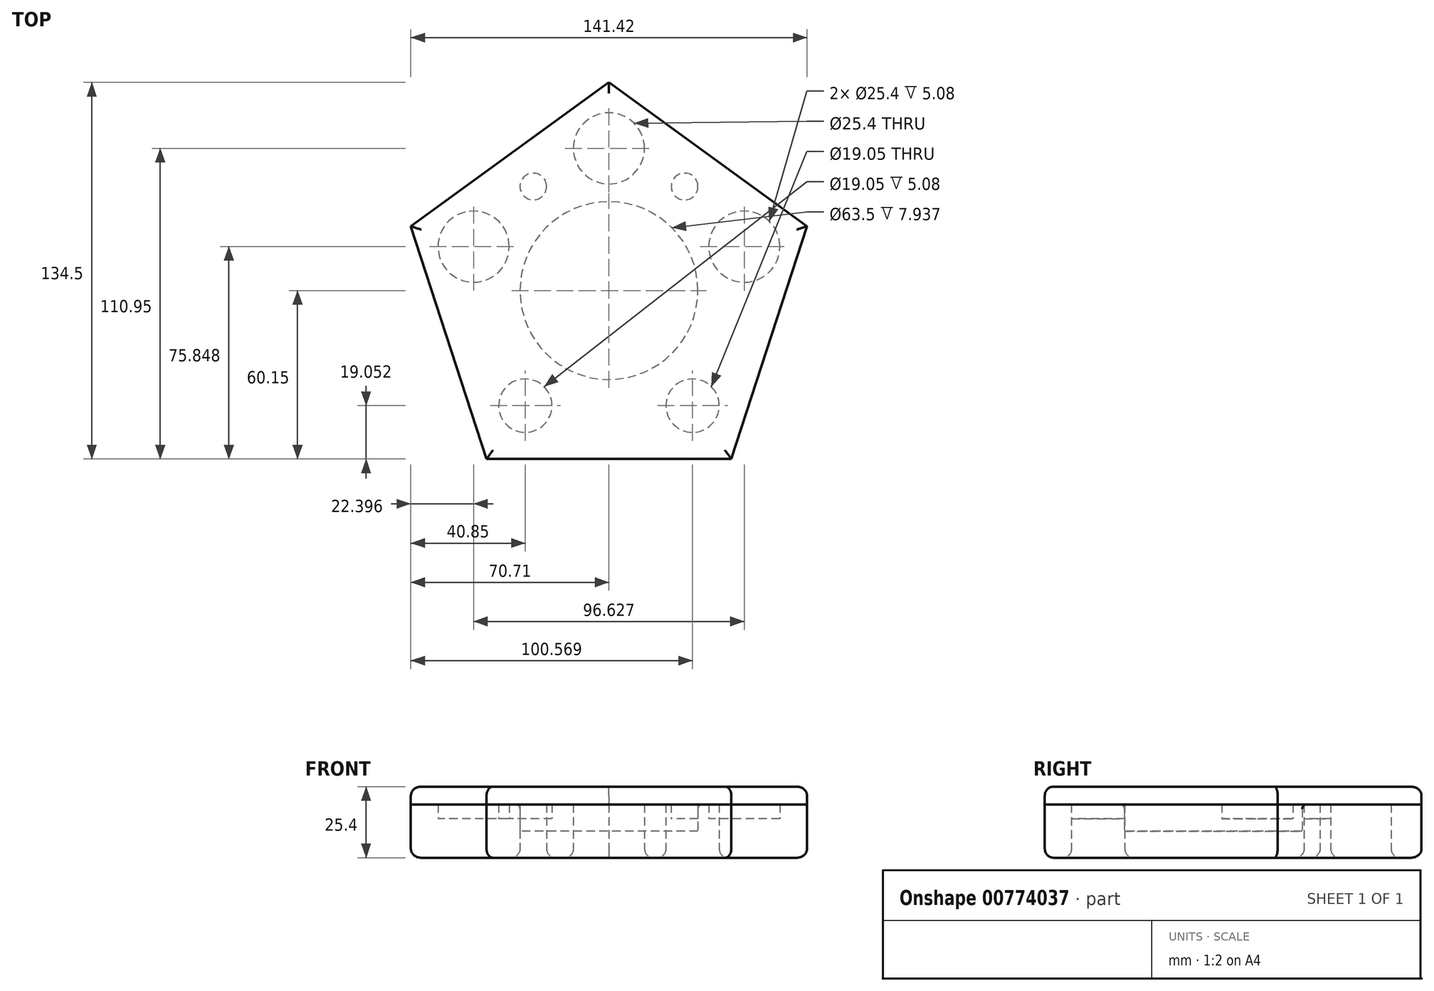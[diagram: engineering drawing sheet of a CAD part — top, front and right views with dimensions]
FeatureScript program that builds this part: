
annotation { "Feature Type Name" : "Feature", "Feature Type Description" : "" }
export const myFeature = defineFeature(function(context is Context, id is Id, definition is map)
    precondition{}
    {
        {
            var Q0;
            Q0=qCreatedBy(makeId("Top.planeOp"),FACE);
            var sketch = newSketch(context, id + "F0", { "sketchPlane" : qUnion([Q0])});
            skLineSegment(sketch, "E0", {"start": v(43.7, -60.15) * mm, "end": v(-43.7, -60.15) * mm});
            skLineSegment(sketch, "E1", {"start": v(-43.7, -60.15) * mm, "end": v(-70.7, 22.97) * mm});
            skLineSegment(sketch, "E2", {"start": v(-70.7, 22.97) * mm, "end": v(0, 74.35) * mm});
            skLineSegment(sketch, "E3", {"start": v(0, 74.35) * mm, "end": v(70.7, 22.97) * mm});
            skLineSegment(sketch, "E4", {"start": v(70.7, 22.97) * mm, "end": v(43.7, -60.15) * mm});
            skCircle(sketch, "E5", {"center": v(0, 0) * mm, "radius": 31.75 * mm});
            skLineSegment(sketch, "E6", {"start": v(-43.7, -60.15) * mm, "end": v(35.35, 48.66) * mm, "construction": true});
            skLineSegment(sketch, "E7", {"start": v(-35.35, 48.66) * mm, "end": v(43.7, -60.15) * mm, "construction": true});
            skLineSegment(sketch, "E8", {"start": v(-70.7, 22.97) * mm, "end": v(57.2, -18.59) * mm, "construction": true});
            skLineSegment(sketch, "E9", {"start": v(0, 74.35) * mm, "end": v(0, -60.15) * mm, "construction": true});
            skLineSegment(sketch, "E10", {"start": v(35.35, 48.66) * mm, "end": v(18.66, 25.69) * mm, "construction": true});
            skCircle(sketch, "E11", {"center": v(-29.86, -41.1) * mm, "radius": 9.53 * mm});
            skCircle(sketch, "E12.MirrorC", {"center": v(29.86, -41.1) * mm, "radius": 9.53 * mm});
            skCircle(sketch, "E13", {"center": v(-48.31, 15.7) * mm, "radius": 12.7 * mm});
            skCircle(sketch, "E14", {"center": v(27, 37.17) * mm, "radius": 4.76 * mm});
            skCircle(sketch, "E15.MirrorC", {"center": v(-27, 37.17) * mm, "radius": 4.76 * mm});
            skLineSegment(sketch, "E16", {"start": v(-29.86, -50.62) * mm, "end": v(-29.86, -60.15) * mm, "construction": true});
            skLineSegment(sketch, "E17", {"start": v(-18.66, -25.69) * mm, "end": v(-24.26, -33.4) * mm, "construction": true});
            skCircle(sketch, "E18.MirrorC", {"center": v(0, 50.8) * mm, "radius": 12.7 * mm});
            skCircle(sketch, "E19.MirrorC", {"center": v(48.31, 15.7) * mm, "radius": 12.7 * mm});
            skLineSegment(sketch, "E20", {"start": v(70.7, 22.97) * mm, "end": v(-57.2, -18.59) * mm, "construction": true});
            skSolve(sketch);
        }
        {
            var Q0;
            Q0=makeQuery(id+"F0.imprint","IMPRINT",FACE,{"disambiguationData":[TD([[makeQuery(id+"F0.imprint","IMPRINT",EDGE,{"derivedFrom":sQuery(id+"F0.wireOp",EDGE,"E0")}),-1.0]])]});
            extrude(context, id + "F1", {"entities" : qUnion([Q0]), "depth" : 19.05 * mm, "offsetDistance" : 25.4 * mm});
        }
        {
            var Q0;
            Q0=makeQuery(id+"F0.imprint","IMPRINT",FACE,{"disambiguationData":[TD([[makeQuery(id+"F0.imprint","IMPRINT",EDGE,{"derivedFrom":sQuery(id+"F0.wireOp",EDGE,"E13")}),1.0]])]});
            var Q1;
            Q1=makeQuery(id+"F0.imprint","IMPRINT",FACE,{"disambiguationData":[TD([[makeQuery(id+"F0.imprint","IMPRINT",EDGE,{"derivedFrom":sQuery(id+"F0.wireOp",EDGE,"E18.MirrorC")}),-1.0]])]});
            var Q2;
            Q2=makeQuery(id+"F0.imprint","IMPRINT",FACE,{"disambiguationData":[TD([[makeQuery(id+"F0.imprint","IMPRINT",EDGE,{"derivedFrom":sQuery(id+"F0.wireOp",EDGE,"E19.MirrorC")}),1.0]])]});
            var Q3;
            Q3=makeQuery(id+"F0.imprint","IMPRINT",FACE,{"disambiguationData":[TD([[makeQuery(id+"F0.imprint","IMPRINT",EDGE,{"derivedFrom":sQuery(id+"F0.wireOp",EDGE,"E12.MirrorC")}),-1.0]])]});
            var Q4;
            Q4=makeQuery(id+"F0.imprint","IMPRINT",FACE,{"disambiguationData":[TD([[makeQuery(id+"F0.imprint","IMPRINT",EDGE,{"derivedFrom":sQuery(id+"F0.wireOp",EDGE,"E11")}),1.0]])]});
            var Q5;
            Q5=makeQuery(id+"F0.imprint","IMPRINT",FACE,{"disambiguationData":[TD([[makeQuery(id+"F0.imprint","IMPRINT",EDGE,{"derivedFrom":sQuery(id+"F0.wireOp",EDGE,"E15.MirrorC")}),-1.0]])]});
            var Q6;
            Q6=makeQuery(id+"F0.imprint","IMPRINT",FACE,{"disambiguationData":[TD([[makeQuery(id+"F0.imprint","IMPRINT",EDGE,{"derivedFrom":sQuery(id+"F0.wireOp",EDGE,"E14")}),1.0]])]});
            extrude(context, id + "F2", {"entities" : qUnion([Q0, Q1, Q2, Q3, Q4, Q5, Q6]), "operationType" : NewBodyOperationType.ADD, "depth" : 13.97 * mm, "offsetDistance" : 25.4 * mm});
        }
        {
            var Q0;
            Q0=makeQuery(id+"F0.imprint","IMPRINT",FACE,{"disambiguationData":[TD([[makeQuery(id+"F0.imprint","IMPRINT",EDGE,{"derivedFrom":sQuery(id+"F0.wireOp",EDGE,"E5")}),1.0]])]});
            extrude(context, id + "F3", {"entities" : qUnion([Q0]), "operationType" : NewBodyOperationType.ADD, "depth" : 9.52 * mm, "offsetDistance" : 25.4 * mm});
        }
        {
            var Q0;
            Q0=makeQuery(id+"F1.opExtrude","CAP_EDGE",EDGE,{"disambiguationData":[OSD([sQuery(id+"F0.wireOp",EDGE,"2c56e169-6147-4ef5-a7f6-485da12cc7880.MirrorC")])],"isStart":false});
            var Q1;
            Q1=makeQuery(id+"F1.opExtrude","CAP_EDGE",EDGE,{"disambiguationData":[OSD([sQuery(id+"F0.wireOp",EDGE,"8a1fa69a-fd36-4c4c-a845-0cc6a3f8c8e40.MirrorC")])],"isStart":false});
            var Q2;
            Q2=makeQuery(id+"F1.opExtrude","CAP_EDGE",EDGE,{"disambiguationData":[OSD([sQuery(id+"F0.wireOp",EDGE,"6bcb9663-89c8-408a-a2a6-6b7f16ca505f0.MirrorC")])],"isStart":false});
            var Q3;
            Q3=makeQuery(id+"F1.opExtrude","CAP_EDGE",EDGE,{"disambiguationData":[OSD([sQuery(id+"F0.wireOp",EDGE,"453847c8-7987-4a18-b065-9be6280f060c0.MirrorC")])],"isStart":false});
            var Q4;
            Q4=makeQuery(id+"F1.opExtrude","CAP_EDGE",EDGE,{"disambiguationData":[OSD([sQuery(id+"F0.wireOp",EDGE,"E5")])],"isStart":false});
            fillet(context, id + "F4", {"entities" : qUnion([Q0, Q1, Q2, Q3, Q4]), "radius" : 1.59 * mm, "tangentPropagation" : true, "allowEdgeOverflow" : false});
        }
        {
            var Q0;
            {var subQ0=sQuery(id+"F0.wireOp",EDGE,"E5");var subQ1=sQuery(id+"F0.wireOp",EDGE,"e476348e-1649-4b46-bcd3-dc1ea815057a.3.0");var subQ2=sQuery(id+"F0.wireOp",EDGE,"e476348e-1649-4b46-bcd3-dc1ea815057a.2.0");var subQ3=sQuery(id+"F0.wireOp",EDGE,"e476348e-1649-4b46-bcd3-dc1ea815057a.1.0");var subQ4=sQuery(id+"F0.wireOp",EDGE,"MC0p9ZNr-SyYg-DCem-tr0t-xkaBVnFnONXK");var subQ5=sQuery(id+"F0.wireOp",EDGE,"2c56e169-6147-4ef5-a7f6-485da12cc7880.MirrorC");var subQ6=sQuery(id+"F0.wireOp",EDGE,"8a1fa69a-fd36-4c4c-a845-0cc6a3f8c8e40.MirrorC");var subQ7=sQuery(id+"F0.wireOp",EDGE,"6bcb9663-89c8-408a-a2a6-6b7f16ca505f0.MirrorC");var subQ8=sQuery(id+"F0.wireOp",EDGE,"453847c8-7987-4a18-b065-9be6280f060c0.MirrorC");Q0=makeQuery(id+"F3.boolean.opBoolean","MERGE",FACE,{"derivedFrom":[makeQuery(id+"FqOStmo2R99PwcP_1.boolean.opBoolean","MERGE",FACE,{"derivedFrom":[makeQuery(id+"F2.boolean.opBoolean","MERGE",FACE,{"derivedFrom":[makeQuery(id+"F1.opExtrude","CAP_FACE",FACE,{"disambiguationData":[OSD([sQuery(id+"F0.wireOp",EDGE,"E0"),sQuery(id+"F0.wireOp",EDGE,"E1"),sQuery(id+"F0.wireOp",EDGE,"E2"),sQuery(id+"F0.wireOp",EDGE,"E3"),sQuery(id+"F0.wireOp",EDGE,"E4"),subQ0,subQ8,subQ7,subQ6,subQ5,subQ4,subQ3,subQ2,subQ1])],"isStart":true}),makeQuery(id+"F2.opExtrude","CAP_FACE",FACE,{"disambiguationData":[OSD([subQ8])],"isStart":true}),makeQuery(id+"F2.opExtrude","CAP_FACE",FACE,{"disambiguationData":[OSD([subQ7])],"isStart":true}),makeQuery(id+"F2.opExtrude","CAP_FACE",FACE,{"disambiguationData":[OSD([subQ6])],"isStart":true}),makeQuery(id+"F2.opExtrude","CAP_FACE",FACE,{"disambiguationData":[OSD([subQ5])],"isStart":true})]}),makeQuery(id+"FqOStmo2R99PwcP_1.opExtrude","CAP_FACE",FACE,{"disambiguationData":[OSD([subQ4])],"isStart":true}),makeQuery(id+"FqOStmo2R99PwcP_1.opExtrude","CAP_FACE",FACE,{"disambiguationData":[OSD([subQ3])],"isStart":true}),makeQuery(id+"FqOStmo2R99PwcP_1.opExtrude","CAP_FACE",FACE,{"disambiguationData":[OSD([subQ2])],"isStart":true}),makeQuery(id+"FqOStmo2R99PwcP_1.opExtrude","CAP_FACE",FACE,{"disambiguationData":[OSD([subQ1])],"isStart":true})]}),makeQuery(id+"F3.opExtrude","CAP_FACE",FACE,{"disambiguationData":[OSD([subQ0])],"isStart":true})]});}
            fillet(context, id + "F5", {"entities" : qUnion([Q0]), "radius" : 3.17 * mm, "tangentPropagation" : true, "allowEdgeOverflow" : false});
        }
        {
            var Q0;
            Q0=makeQuery(id+"F1.opExtrude","CAP_FACE",FACE,{"disambiguationData":[OSD([sQuery(id+"F0.wireOp",EDGE,"E0"),sQuery(id+"F0.wireOp",EDGE,"E1"),sQuery(id+"F0.wireOp",EDGE,"E2"),sQuery(id+"F0.wireOp",EDGE,"E3"),sQuery(id+"F0.wireOp",EDGE,"E4"),sQuery(id+"F0.wireOp",EDGE,"E5"),sQuery(id+"F0.wireOp",EDGE,"453847c8-7987-4a18-b065-9be6280f060c0.MirrorC"),sQuery(id+"F0.wireOp",EDGE,"6bcb9663-89c8-408a-a2a6-6b7f16ca505f0.MirrorC"),sQuery(id+"F0.wireOp",EDGE,"8a1fa69a-fd36-4c4c-a845-0cc6a3f8c8e40.MirrorC"),sQuery(id+"F0.wireOp",EDGE,"2c56e169-6147-4ef5-a7f6-485da12cc7880.MirrorC"),sQuery(id+"F0.wireOp",EDGE,"MC0p9ZNr-SyYg-DCem-tr0t-xkaBVnFnONXK"),sQuery(id+"F0.wireOp",EDGE,"e476348e-1649-4b46-bcd3-dc1ea815057a.1.0"),sQuery(id+"F0.wireOp",EDGE,"e476348e-1649-4b46-bcd3-dc1ea815057a.2.0"),sQuery(id+"F0.wireOp",EDGE,"e476348e-1649-4b46-bcd3-dc1ea815057a.3.0")])],"isStart":false});
            var sketch = newSketch(context, id + "F6", { "sketchPlane" : qUnion([Q0])});
            skLineSegment(sketch, "E21.0", {"start": v(-43.7, -60.15) * mm, "end": v(-70.7, 22.97) * mm});
            skLineSegment(sketch, "E22.0", {"start": v(43.7, -60.15) * mm, "end": v(-43.7, -60.15) * mm});
            skLineSegment(sketch, "E23.0", {"start": v(70.7, 22.97) * mm, "end": v(43.7, -60.15) * mm});
            skLineSegment(sketch, "E24.0", {"start": v(0, 74.35) * mm, "end": v(70.7, 22.97) * mm});
            skLineSegment(sketch, "E25.0", {"start": v(-70.7, 22.97) * mm, "end": v(0, 74.35) * mm});
            skSolve(sketch);
        }
        {
            var Q0;
            Q0 = qSketchRegion(id + "F6", true);
            extrude(context, id + "F7", {"entities" : qUnion([Q0]), "depth" : 6.35 * mm, "offsetDistance" : 25.4 * mm});
        }
        {
            var Q0;
            Q0=makeQuery(id+"F7.opExtrude","CAP_FACE",FACE,{"disambiguationData":[OSD([sQuery(id+"F6.wireOp",EDGE,"E21.0"),sQuery(id+"F6.wireOp",EDGE,"E22.0"),sQuery(id+"F6.wireOp",EDGE,"E23.0"),sQuery(id+"F6.wireOp",EDGE,"E24.0"),sQuery(id+"F6.wireOp",EDGE,"E25.0")])],"isStart":false});
            fillet(context, id + "F8", {"entities" : qUnion([Q0]), "radius" : 3.17 * mm, "tangentPropagation" : true, "allowEdgeOverflow" : false});
        }
    });
